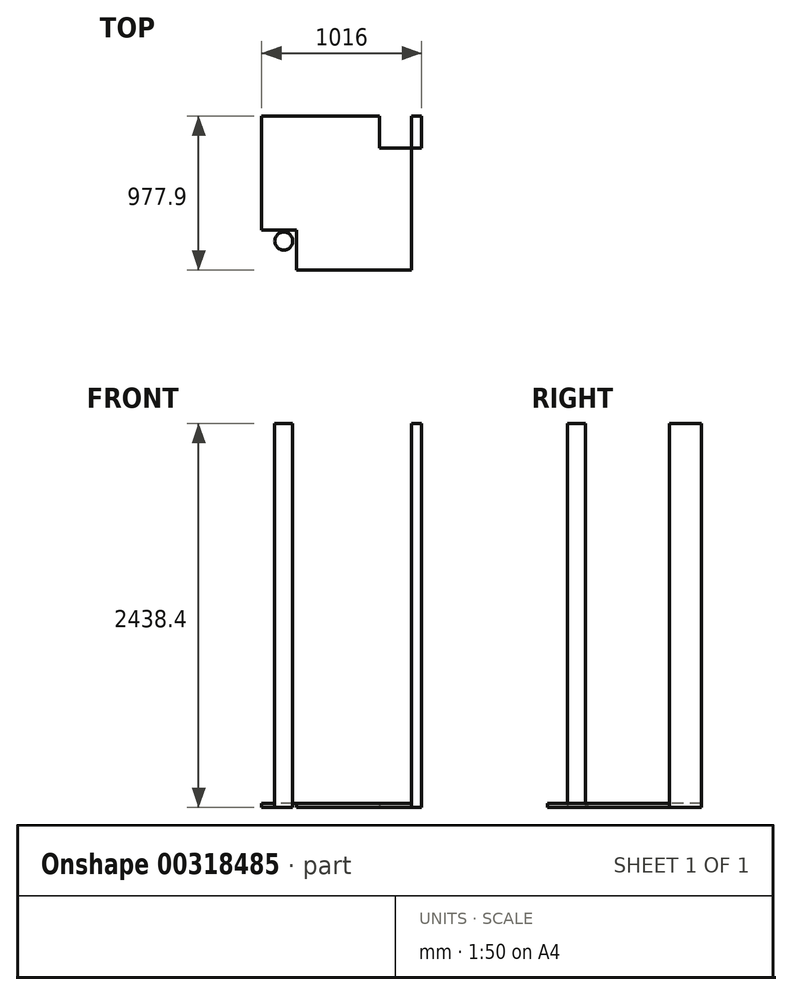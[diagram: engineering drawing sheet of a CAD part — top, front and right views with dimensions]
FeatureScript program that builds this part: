
annotation { "Feature Type Name" : "Feature", "Feature Type Description" : "" }
export const myFeature = defineFeature(function(context is Context, id is Id, definition is map)
    precondition{}
    {
        {
            var Q0;
            Q0=qCreatedBy(makeId("Top.planeOp"),FACE);
            var sketch = newSketch(context, id + "F0", { "sketchPlane" : qUnion([Q0])});
            skLineSegment(sketch, "E0.bottom", {"start": v(-516.81, 552.88) * mm, "end": v(499.19, 552.88) * mm});
            skLineSegment(sketch, "E0.top", {"start": v(-516.81, -463.12) * mm, "end": v(499.19, -463.12) * mm});
            skLineSegment(sketch, "E0.left", {"start": v(-516.81, 552.88) * mm, "end": v(-516.81, -463.12) * mm});
            skLineSegment(sketch, "E0.right", {"start": v(499.19, 552.88) * mm, "end": v(499.19, -463.12) * mm});
            skLineSegment(sketch, "E1", {"start": v(435.69, 552.88) * mm, "end": v(435.69, 349.68) * mm});
            skLineSegment(sketch, "E2", {"start": v(435.69, 349.68) * mm, "end": v(499.19, 349.68) * mm});
            skCircle(sketch, "E3", {"center": v(-377.11, -240.87) * mm, "radius": 57.15 * mm});
            skLineSegment(sketch, "E4", {"start": v(232.49, 552.88) * mm, "end": v(232.49, 349.68) * mm});
            skLineSegment(sketch, "E5", {"start": v(232.49, 349.68) * mm, "end": v(435.69, 349.68) * mm});
            skLineSegment(sketch, "E6", {"start": v(-516.81, -425.02) * mm, "end": v(-294.56, -425.02) * mm});
            skLineSegment(sketch, "E7", {"start": v(-294.56, -425.02) * mm, "end": v(-294.56, -171.02) * mm});
            skLineSegment(sketch, "E8", {"start": v(-294.56, -171.02) * mm, "end": v(-516.81, -171.02) * mm});
            skLineSegment(sketch, "E9", {"start": v(-294.56, -425.02) * mm, "end": v(435.69, -425.02) * mm});
            skLineSegment(sketch, "E10", {"start": v(435.69, -425.02) * mm, "end": v(435.69, 349.68) * mm});
            skSolve(sketch);
        }
        {
            var Q0;
            {var subQ3=sQuery(id+"F0.wireOp",EDGE,"E1");Q0=makeQuery(id+"F0.imprint","IMPRINT",FACE,{"disambiguationData":[TD([[makeQuery(id+"F0.imprint","IMPRINT",EDGE,{"derivedFrom":subQ3}),1.0]])]});}
            var Q1;
            Q1=makeQuery(id+"F0.imprint","IMPRINT",FACE,{"disambiguationData":[TD([[makeQuery(id+"F0.imprint","IMPRINT",EDGE,{"derivedFrom":sQuery(id+"F0.wireOp",EDGE,"E3")}),1.0]])]});
            extrude(context, id + "F1", {"entities" : qUnion([Q0, Q1]), "depth" : 2438.4 * mm});
        }
        {
            var Q0;
            {var subQ0=sQuery(id+"F0.wireOp",EDGE,"E4");Q0=makeQuery(id+"F0.imprint","IMPRINT",FACE,{"disambiguationData":[TD([[makeQuery(id+"F0.imprint","IMPRINT",EDGE,{"derivedFrom":subQ0}),-1.0]])]});}
            extrude(context, id + "F2", {"entities" : qUnion([Q0]), "depth" : 25.4 * mm});
        }
    });
